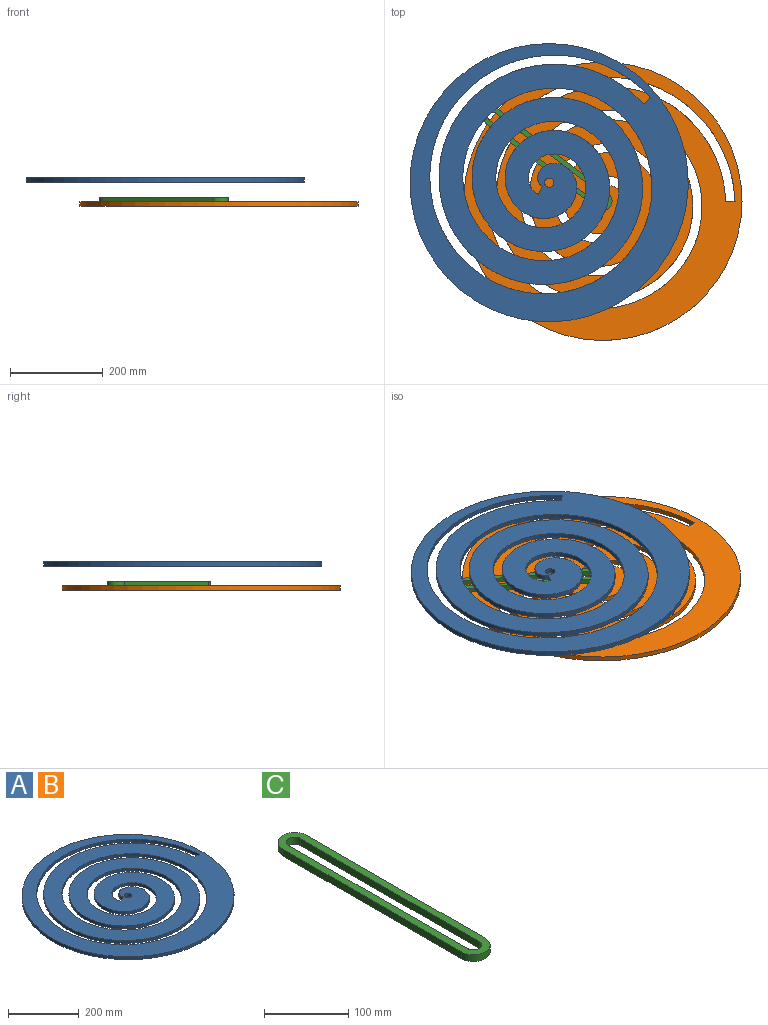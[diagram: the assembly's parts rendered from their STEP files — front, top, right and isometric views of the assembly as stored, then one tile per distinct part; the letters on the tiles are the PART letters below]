
ASSEMBLY  parts=3 mates=2
PART A: 8 faces, bbox 600x600x20 mm
  f0: plane 600x600mm, normal (0,0,-1), area 216242mm2, adj f1,f3,f4,f5,f6,f7
  f1: cylinder r=300mm len=600mm, axis (0,0,-1), area 18849.6mm2, adj f0,f2
  f2: plane 600x600mm, normal (0,0,1), area 216086.8mm2, adj f1,f3,f4,f5,f6,f7
  f3: plane 20x10mm, normal (0,1,0), area 200mm2, adj f0,f2,f5,f6
  f4: plane 18.53x10mm, normal (-0.38,0.93,0), area 200mm2, adj f0,f2,f5,f6
  f5: bspline ~494.97x460.97mm, area 30875.1mm2, adj f0,f2,f3,f4
  f6: bspline ~534.93x501.13mm, area 35356.9mm2, adj f0,f2,f3,f4
  f7: cylinder r=10mm len=20mm, axis (0,0,1), area 628.3mm2, adj f0,f2
PART B: same geometry as A
PART C: 10 faces, bbox 40x340x10 mm
  f0: plane 340x40mm, normal (0,0,1), area 6942.5mm2, adj f2,f3,f4,f5,f6,f7,f8,f9
  f1: plane 340x40mm, normal (0,0,-1), area 6942.5mm2, adj f2,f3,f4,f5,f6,f7,f8,f9
  f2: cylinder r=20mm len=40mm, axis (0,0,-1), area 628.3mm2, adj f0,f1,f3,f5
  f3: plane 300x10mm, normal (1,0,0), area 3000mm2, adj f0,f1,f2,f4
  f4: cylinder r=20mm len=40mm, axis (0,0,-1), area 628.3mm2, adj f0,f1,f3,f5
  f5: plane 300x10mm, normal (-1,0,0), area 3000mm2, adj f0,f1,f2,f4
  f6: cylinder r=10mm len=20mm, axis (0,0,1), area 314.2mm2, adj f0,f1,f7,f8
  f7: plane 300x10mm, normal (1,0,0), area 3000mm2, adj f0,f1,f6,f9
  f8: plane 300x10mm, normal (-1,0,0), area 3000mm2, adj f0,f1,f6,f9
  f9: cylinder r=10mm len=20mm, axis (0,0,1), area 314.2mm2, adj f0,f1,f7,f8
PLACE A rot(axis=(0,0,1),39.9deg) t=(-124.76,-16.86,-99.83)mm
PLACE B t=(-8.9,-56.88,-151.75)mm fixed
PLACE C rot(axis=(0,0,-1),127.5deg) t=(-127.95,34.37,-141.75)mm
MATE parallel C.f0 <-> A.f0  axis (0,0,1) through (-127.95,34.37,-136.75)mm
MATE revolute B.f7 <-> C.f4  axis (0,0,1) through (-8.9,-56.88,-146.75)mm
